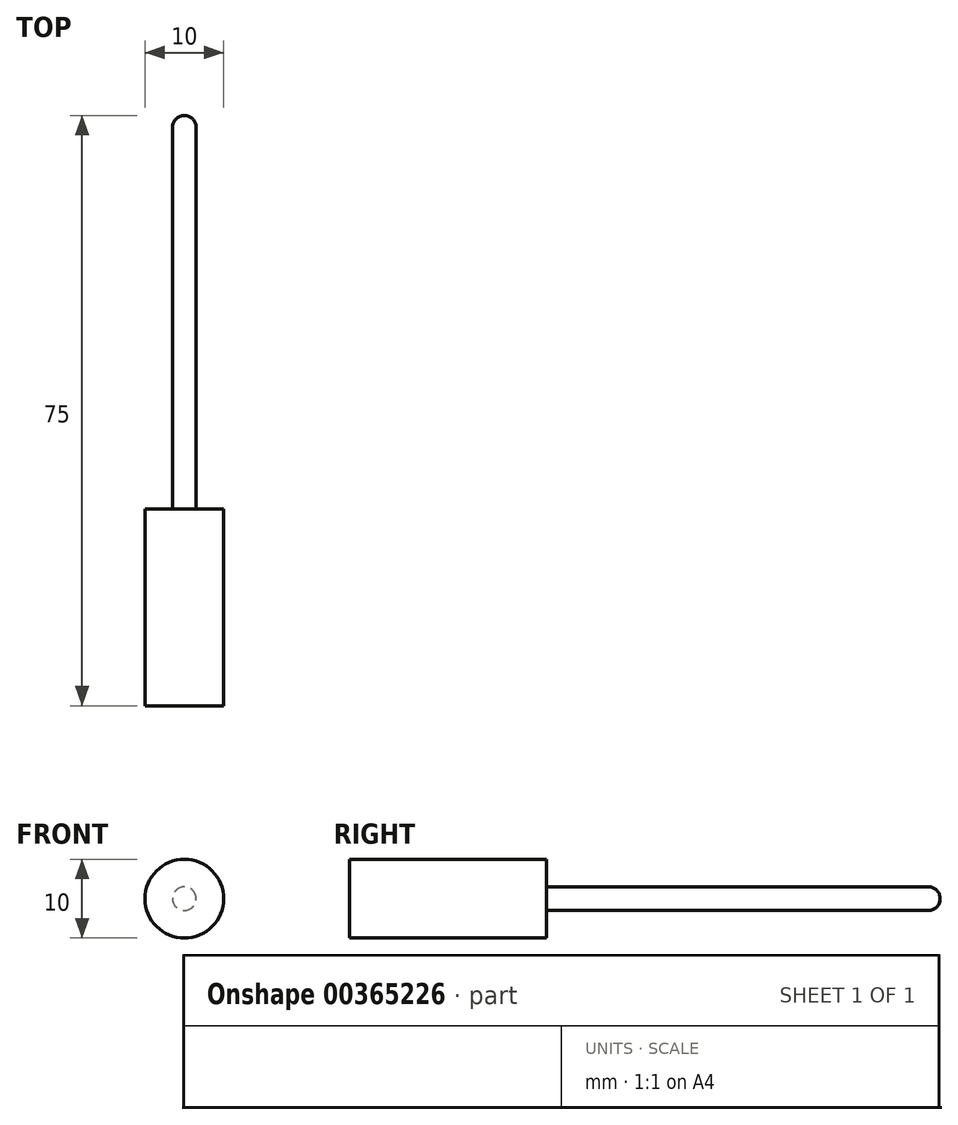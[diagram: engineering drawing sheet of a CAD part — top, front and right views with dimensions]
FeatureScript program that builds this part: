
annotation { "Feature Type Name" : "Feature", "Feature Type Description" : "" }
export const myFeature = defineFeature(function(context is Context, id is Id, definition is map)
    precondition{}
    {
        {
            var Q0;
            Q0=qCreatedBy(makeId("Front.planeOp"),FACE);
            var sketch = newSketch(context, id + "F0", { "sketchPlane" : qUnion([Q0])});
            skCircle(sketch, "E0", {"center": v(0, 0) * mm, "radius": 1.5 * mm});
            skSolve(sketch);
        }
        {
            var Q0;
            Q0 = qSketchRegion(id + "F0", true);
            extrude(context, id + "F1", {"entities" : qUnion([Q0]), "oppositeDirection" : true, "depth" : 50 * mm});
        }
        {
            var Q0;
            Q0=qCreatedBy(makeId("Front.planeOp"),FACE);
            var sketch = newSketch(context, id + "F2", { "sketchPlane" : qUnion([Q0])});
            skCircle(sketch, "E1", {"center": v(0, 0) * mm, "radius": 5 * mm});
            skSolve(sketch);
        }
        {
            var Q0;
            Q0 = qSketchRegion(id + "F2", true);
            extrude(context, id + "F3", {"entities" : qUnion([Q0]), "operationType" : NewBodyOperationType.ADD, "depth" : 25 * mm});
        }
        {
            var Q0;
            Q0=makeQuery(id+"F1.opExtrude","CAP_EDGE",EDGE,{"disambiguationData":[OSD([sQuery(id+"F0.wireOp",EDGE,"E0")])],"isStart":false});
            fillet(context, id + "F4", {"entities" : qUnion([Q0]), "radius" : 1.5 * mm, "tangentPropagation" : true, "allowEdgeOverflow" : false});
        }
    });
